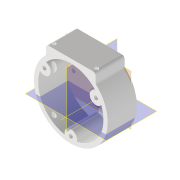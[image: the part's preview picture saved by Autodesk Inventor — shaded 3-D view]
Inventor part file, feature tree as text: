
AUTODESK INVENTOR PART (.ipt)
format: ipt  version: 2022.5 (Build 265521000, 521)  size: 307,200 bytes
history: native  units: mm
features: reference x12, sketch x6, plane x4, extrude x4, projected_geometry x3, other x3, hole x2, fillet x1
ambient origin geometry x8: Origin, YZ Plane, XZ Plane, XY Plane, X Axis, Y Axis, Z Axis, Center Point
bodies: Volumenkörper1 (feature_tree)
feature tree (35):
  plane  "Arbeitsebene1"
  extrude  "Extrusion1"  Depth=2.8mm
  sketch  "Skizze2"  dims[d2=2.8mm d3=12.0mm]
  plane  "Arbeitsebene2"
  extrude  "Extrusion2"  Depth=12.0mm
  plane  "Arbeitsebene4"
  extrude  "Extrusion4"  Depth=3.0mm
  extrude  "Extrusion5"  Depth=2.8mm
  fillet  "Rundung1"  [1 undecoded]
  hole  "Bohrung1"  [1 undecoded]
  hole  "Bohrung2"  [1 undecoded]
  sketch  "Skizze1"  dims[d0=52.0mm d1=2.8mm]
  reference  "Referenz1"
  reference  "Referenz2"
  reference  "Referenz3"
  reference  "Referenz4"
  projected_geometry  "Projizierte Kontur1"
  reference  "Referenz5"
  reference  "Referenz6"
  reference  "Referenz7"
  reference  "Referenz8"
  reference  "Referenz9"
  reference  "Referenz10"
  reference  "Referenz11"
  reference  "Referenz12"
  plane  "Arbeitsebene3"
  other  "Arbeitsachse1"
  sketch  "Skizze6"  dims[d4=1.0mm d5=0.0mm d6=3.0mm]
  sketch  "Skizze7"  dims[d7=3.0mm d8=0.0mm d9=2.8mm d15=90.0deg]
  projected_geometry  "Projizierte Kontur2"
  sketch  "Skizze8"  dims[d26=10.0mm d27=0.0mm d28=35.0mm]
  sketch  "Skizze9"  dims[d30=1.0mm d31=0.0mm d32=2.0mm d33=30.0mm d34=35.0mm d35=2.8mm d36=6.0mm d37=4.0mm d38=2.0mm d39=90.0deg d40=8.0mm d41=20.594885mm d42=3.0mm d43=3.0mm d44=3.0mm d45=3.0mm d46=2.8mm d47=6.0mm d48=6.5mm d49=3.5mm d50=90.0deg d51=30.0mm d52=20.594885mm]
  projected_geometry  "Projizierte Kontur3"
  other  "Planktoscope_Mini_Peristalticpump_new.iam"
  other  "00_Stepper_Motor_28BYJ-48:1"
note: 3 required parameter values undecoded (feature->parameter linkage not recoverable at this tier; creation-order binding heuristic only, values carry confidence <= 0.55)
